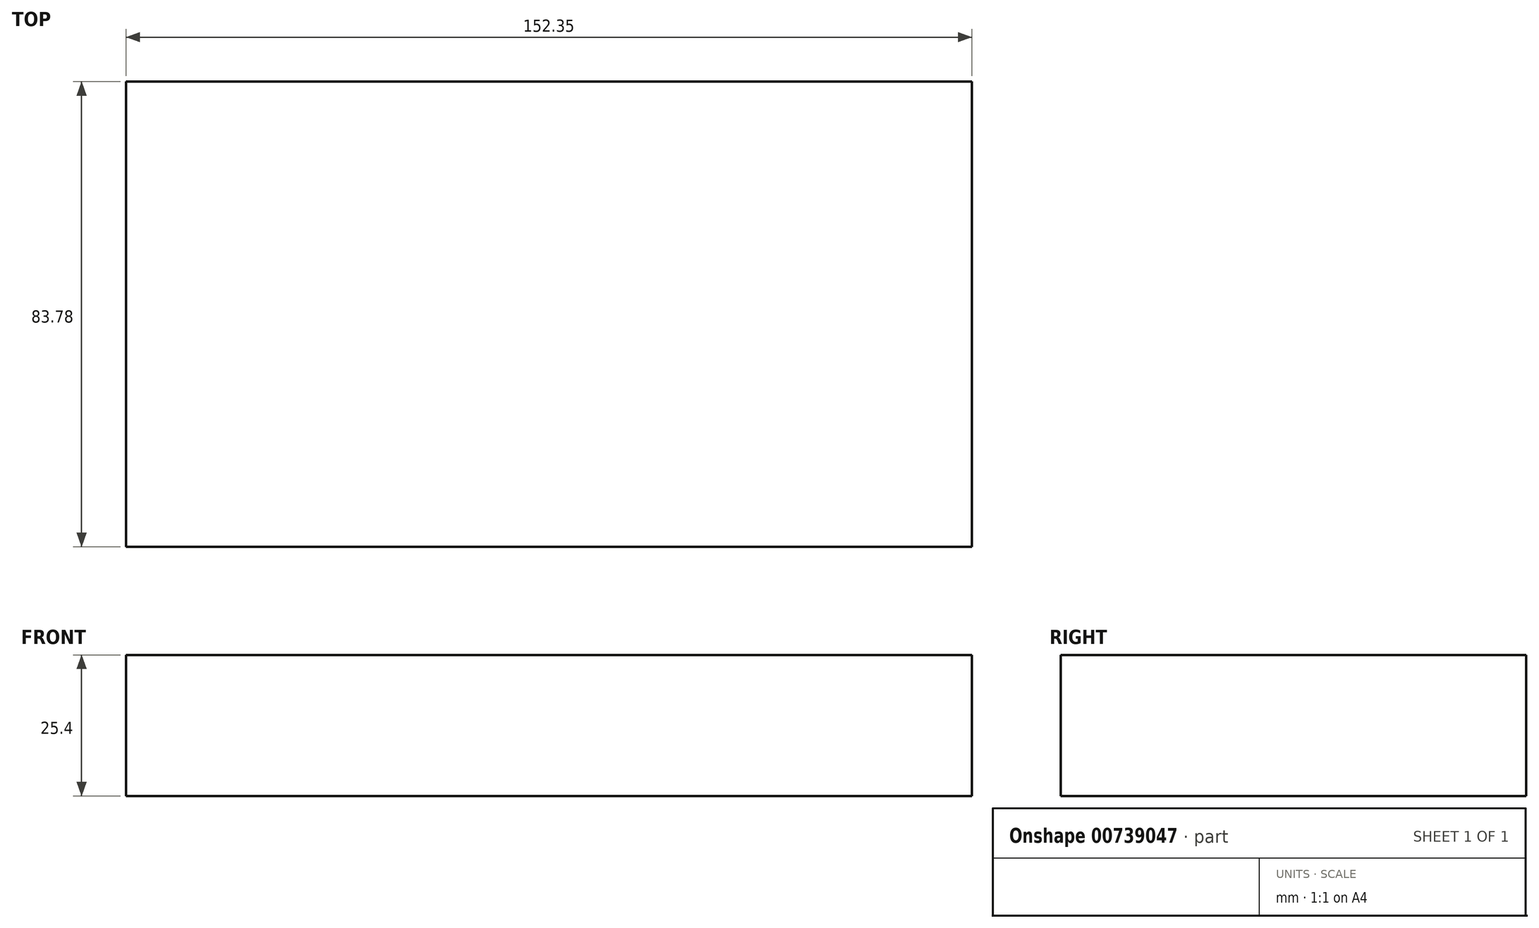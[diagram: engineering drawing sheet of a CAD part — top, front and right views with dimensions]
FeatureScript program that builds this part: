
annotation { "Feature Type Name" : "Feature", "Feature Type Description" : "" }
export const myFeature = defineFeature(function(context is Context, id is Id, definition is map)
    precondition{}
    {
        {
            var Q0;
            Q0=qCreatedBy(makeId("Top.planeOp"),FACE);
            var sketch = newSketch(context, id + "F0", { "sketchPlane" : qUnion([Q0])});
            skLineSegment(sketch, "E0.bottom", {"start": v(-114.6, -35.03) * mm, "end": v(37.75, -35.03) * mm});
            skLineSegment(sketch, "E0.top", {"start": v(-114.6, 48.75) * mm, "end": v(37.75, 48.75) * mm});
            skLineSegment(sketch, "E0.left", {"start": v(-114.6, -35.03) * mm, "end": v(-114.6, 48.75) * mm});
            skLineSegment(sketch, "E0.right", {"start": v(37.75, -35.03) * mm, "end": v(37.75, 48.75) * mm});
            skSolve(sketch);
        }
        {
            var Q0;
            Q0 = qSketchRegion(id + "F0", true);
            extrude(context, id + "F1", {"entities" : qUnion([Q0]), "depth" : 25.4 * mm, "offsetDistance" : 25.4 * mm});
        }
    });
